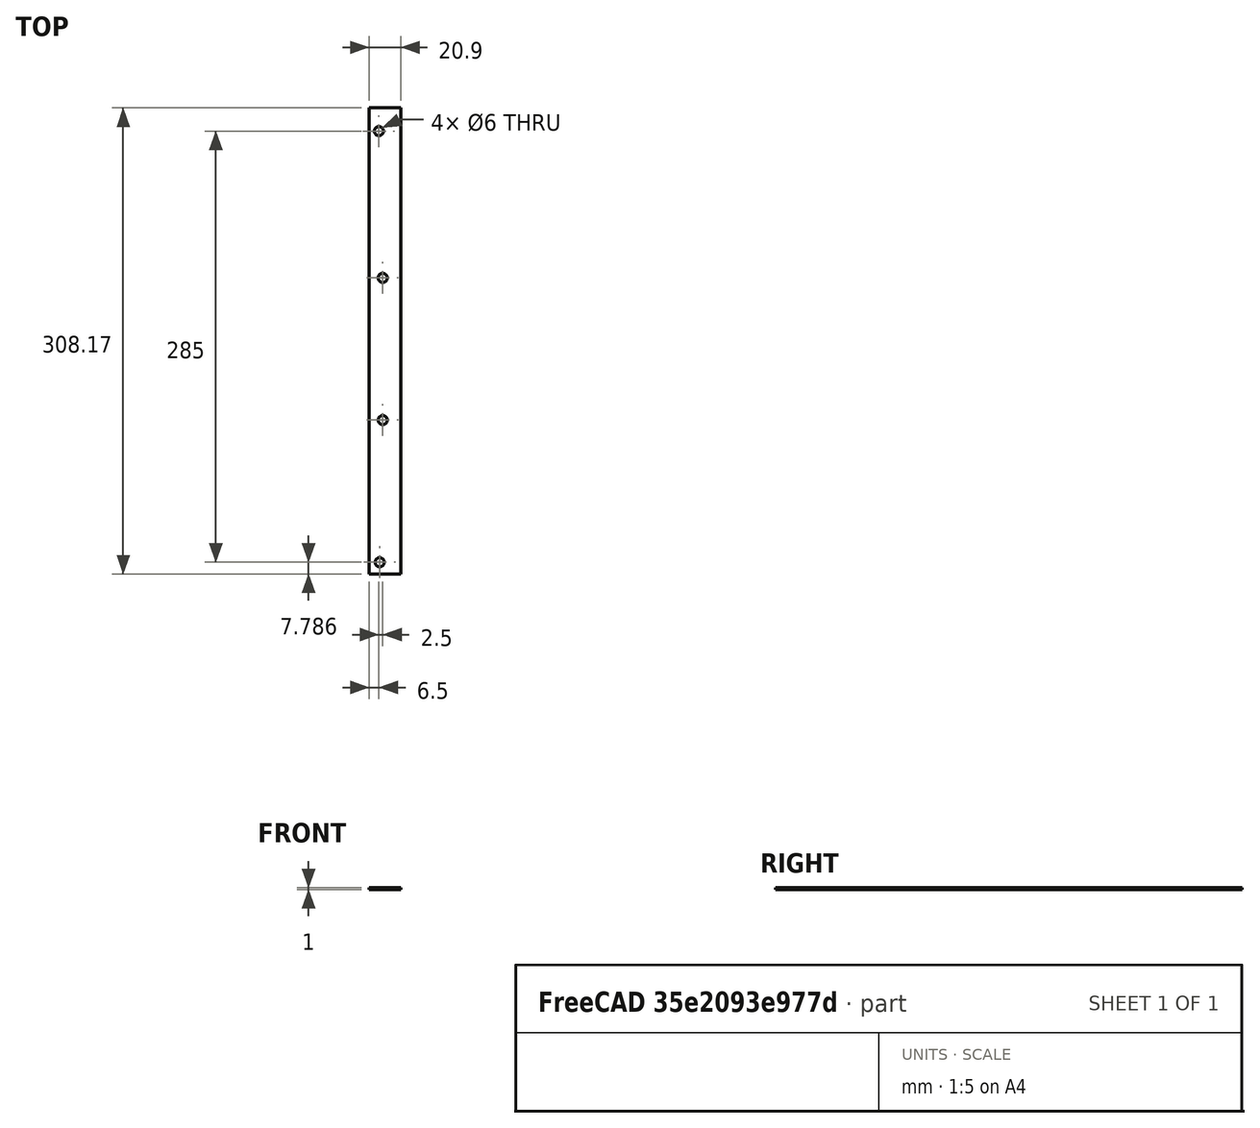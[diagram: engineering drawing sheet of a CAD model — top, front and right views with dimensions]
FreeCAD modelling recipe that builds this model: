
FCSTD DOCUMENT  (FreeCAD 0.22R38261 (Git))
Label: транец
License: All rights reserved
LicenseURL: https://en.wikipedia.org/wiki/All_rights_reserved
objects: Sketcher::SketchObject×1, PartDesign::Pad×1, PartDesign::Body×1
note: 5 computed .brp shape members not serialized (recipe doc carries the construction recipe); baked Part::Feature solids carry a one-line shape summary decoded from their .brp

FEATURE [Sketcher::SketchObject] Sketch
  AttachmentSupport = -> [XY_Plane]
  FullyConstrained = false
  MapMode = 5
  sketch-geometry (8):
    g0: Circle CenterX=-1 CenterY=-1.33407 CenterZ=0 NormalX=0 NormalY=0 NormalZ=1 AngleXU=0 Radius=3
    g1: Circle CenterX=0 CenterY=92.1659 CenterZ=0 NormalX=0 NormalY=0 NormalZ=1 AngleXU=0 Radius=3
    g2: Circle CenterX=0 CenterY=186.166 CenterZ=0 NormalX=0 NormalY=0 NormalZ=1 AngleXU=0 Radius=3
    g3: Circle CenterX=-2.5 CenterY=283.166 CenterZ=0 NormalX=0 NormalY=0 NormalZ=1 AngleXU=0 Radius=3
    g4: LineSegment StartX=-9 StartY=298.671 StartZ=0 EndX=-9 EndY=-9.50409 EndZ=0
    g5: LineSegment StartX=-9 StartY=-9.50409 StartZ=0 EndX=11.9045 EndY=-9.50409 EndZ=0
    g6: LineSegment StartX=11.9045 StartY=-9.50409 StartZ=0 EndX=11.9045 EndY=298.671 EndZ=0
    g7: LineSegment StartX=11.9045 StartY=298.671 StartZ=0 EndX=-9 EndY=298.671 EndZ=0
  constraints (20):
    c: Diameter(g0) = 6
    c: Diameter(g1) = 6
    c: PointOnObject(g1,g-2)
    c: Diameter(g2) = 6
    c: PointOnObject(g2,g-2)
    c: DistanceY(g1,g2) = 94
    c: Diameter(g3) = 6
    c: DistanceY(g2,g3) = 97
    c: Coincident(g4,g5)
    c: Coincident(g5,g6)
    c: Coincident(g6,g7)
    c: Coincident(g7,g4)
    c: Vertical(g4)
    c: Vertical(g6)
    c: Horizontal(g5)
    c: Horizontal(g7)
    c: DistanceY(g0,g1) = 93.5
    c: DistanceX(g3,g-1) = 2.5
    c: DistanceX(g4,g-1) = 9
    c: DistanceX(g0,g-1) = 1
FEATURE [PartDesign::Pad] Pad
  Direction = (0,0,1)
  Length = 1
  Length2 = 10
  Profile = -> Sketch
  ReferenceAxis = -> Sketch [N_Axis]
  Suppressed = false
  Type = 0
FEATURE [PartDesign::Body] Body  label="Тело"
  AllowCompound = false
  Group = -> [Sketch,Pad]
  Origin = -> Origin
  Tip = -> Pad
